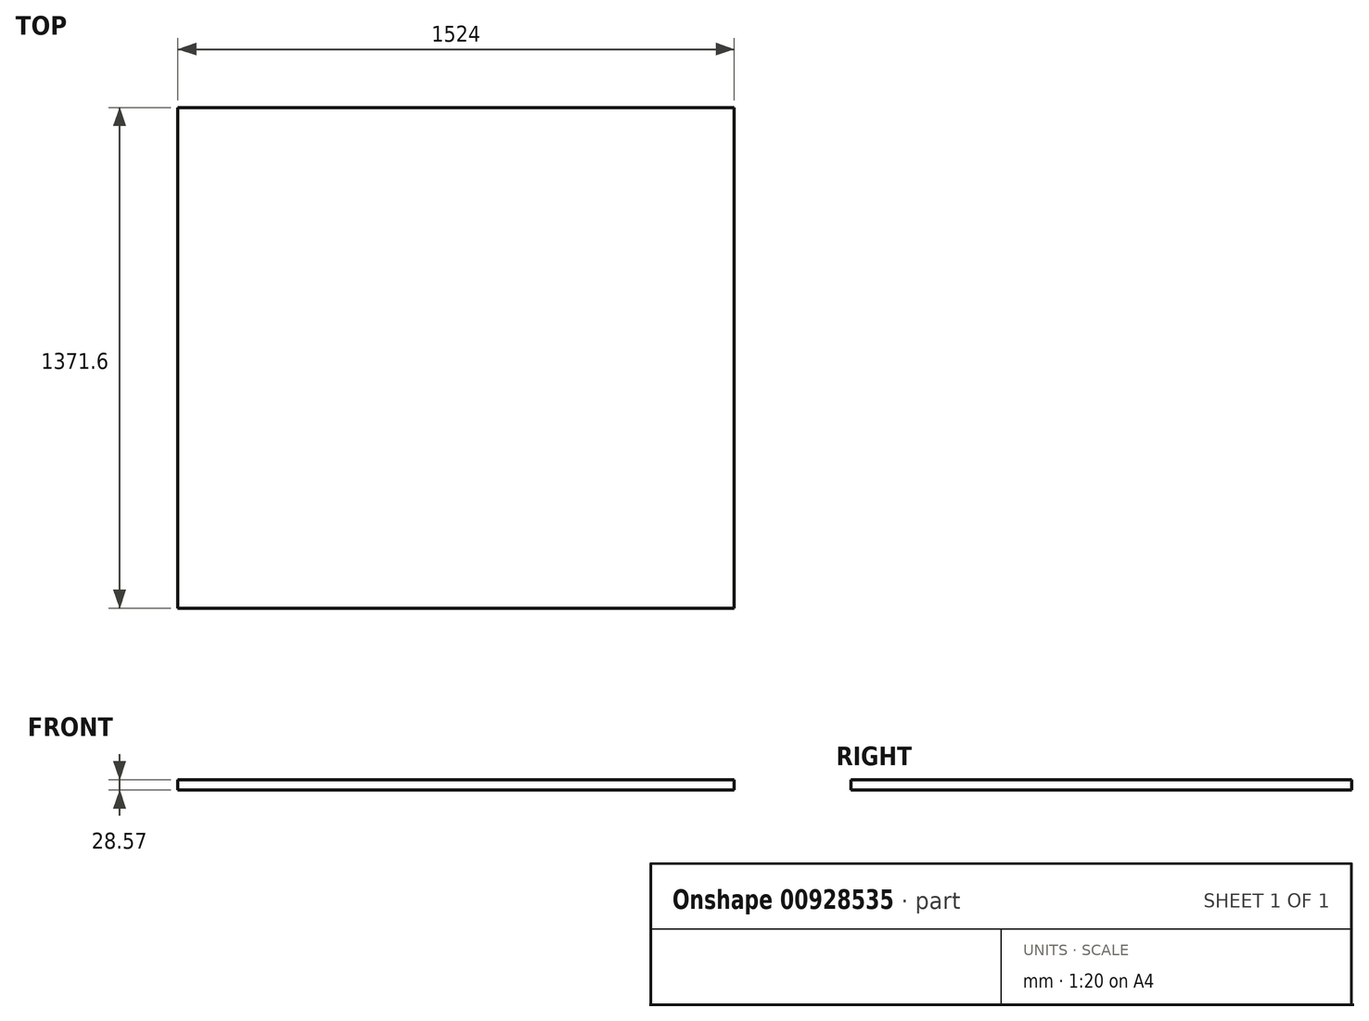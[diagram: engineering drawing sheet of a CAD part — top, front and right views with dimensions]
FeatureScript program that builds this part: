
annotation { "Feature Type Name" : "Feature", "Feature Type Description" : "" }
export const myFeature = defineFeature(function(context is Context, id is Id, definition is map)
    precondition{}
    {
        {
            var Q0;
            Q0=qCreatedBy(makeId("Top.planeOp"),FACE);
            var sketch = newSketch(context, id + "F0", { "sketchPlane" : qUnion([Q0])});
            skLineSegment(sketch, "E0.bottom", {"start": v(762, 685.8) * mm, "end": v(-762, 685.8) * mm});
            skLineSegment(sketch, "E0.top", {"start": v(762, -685.8) * mm, "end": v(-762, -685.8) * mm});
            skLineSegment(sketch, "E0.left", {"start": v(762, 685.8) * mm, "end": v(762, -685.8) * mm});
            skLineSegment(sketch, "E0.right", {"start": v(-762, 685.8) * mm, "end": v(-762, -685.8) * mm});
            skPoint(sketch, "E0.middle", {"position": v(0, 0) * mm});
            skSolve(sketch);
        }
        {
            var Q0;
            Q0=makeQuery(id+"F0.imprint","IMPRINT",FACE,{"disambiguationData":[TD([[makeQuery(id+"F0.imprint","IMPRINT",EDGE,{"derivedFrom":sQuery(id+"F0.wireOp",EDGE,"E0.bottom")}),1.0]])]});
            extrude(context, id + "F1", {"entities" : qUnion([Q0]), "depth" : 28.57 * mm, "offsetDistance" : 25.4 * mm});
        }
    });
